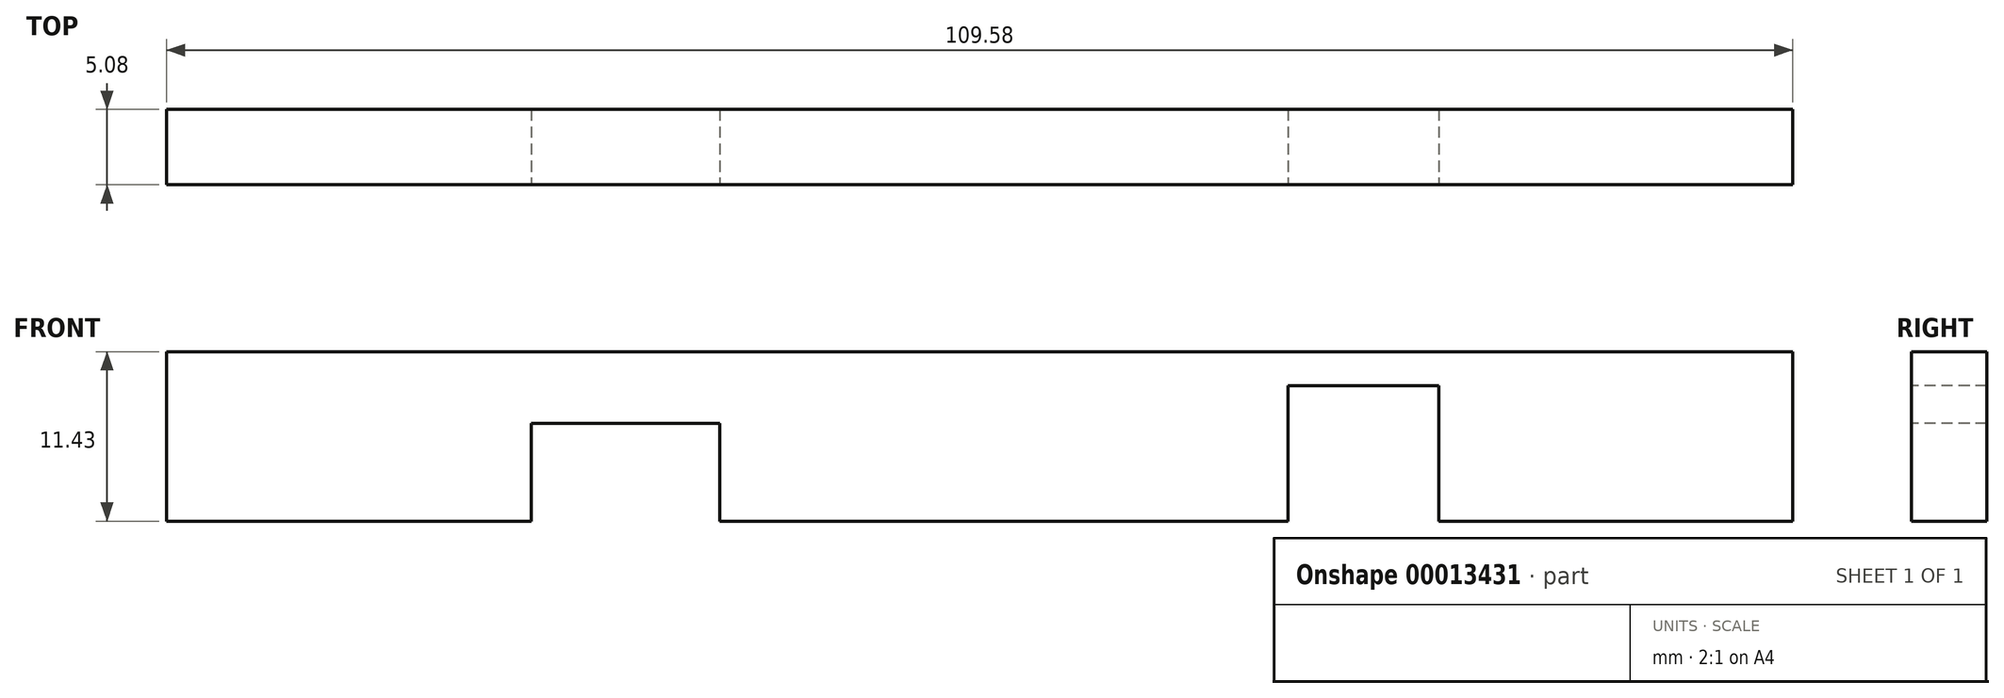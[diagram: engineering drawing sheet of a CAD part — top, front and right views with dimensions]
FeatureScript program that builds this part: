
annotation { "Feature Type Name" : "Feature", "Feature Type Description" : "" }
export const myFeature = defineFeature(function(context is Context, id is Id, definition is map)
    precondition{}
    {
        {
            var Q0;
            Q0=qCreatedBy(makeId("Front.planeOp"),FACE);
            var sketch = newSketch(context, id + "F0", { "sketchPlane" : qUnion([Q0])});
            skLineSegment(sketch, "E0.bottom", {"start": v(0, 0) * mm, "end": v(109.58, 0) * mm});
            skLineSegment(sketch, "E0.top", {"start": v(0, 11.43) * mm, "end": v(109.58, 11.43) * mm});
            skLineSegment(sketch, "E0.left", {"start": v(0, 0) * mm, "end": v(0, 11.43) * mm});
            skLineSegment(sketch, "E0.right", {"start": v(109.58, 0) * mm, "end": v(109.58, 11.43) * mm});
            skSolve(sketch);
        }
        {
            var Q0;
            Q0=qSketchRegion(id+"F0",true);
            extrude(context, id + "F1", {"entities" : qUnion([Q0]), "depth" : 5.08 * mm});
        }
        {
            var Q0;
            Q0=makeQuery(id+"F1.opExtrude","CAP_FACE",FACE,{"disambiguationData":[OSD([sQuery(id+"F0.wireOp",EDGE,"E0.bottom"),sQuery(id+"F0.wireOp",EDGE,"E0.top"),sQuery(id+"F0.wireOp",EDGE,"E0.left"),sQuery(id+"F0.wireOp",EDGE,"E0.right")])],"isStart":false});
            var sketch = newSketch(context, id + "F2", { "sketchPlane" : qUnion([Q0])});
            skLineSegment(sketch, "E1.bottom", {"start": v(24.59, 0) * mm, "end": v(37.29, 0) * mm});
            skLineSegment(sketch, "E1.top", {"start": v(24.59, 6.6) * mm, "end": v(37.29, 6.6) * mm});
            skLineSegment(sketch, "E1.left", {"start": v(24.59, 0) * mm, "end": v(24.59, 6.6) * mm});
            skLineSegment(sketch, "E1.right", {"start": v(37.29, 0) * mm, "end": v(37.29, 6.6) * mm});
            skLineSegment(sketch, "E2.bottom", {"start": v(75.6, 0) * mm, "end": v(85.75, 0) * mm});
            skLineSegment(sketch, "E2.top", {"start": v(75.6, 9.14) * mm, "end": v(85.75, 9.14) * mm});
            skLineSegment(sketch, "E2.left", {"start": v(75.6, 0) * mm, "end": v(75.6, 9.14) * mm});
            skLineSegment(sketch, "E2.right", {"start": v(85.75, 0) * mm, "end": v(85.75, 9.14) * mm});
            skSolve(sketch);
        }
        {
            var Q0;
            Q0 = qSketchRegion(id + "F2", true);
            extrude(context, id + "F3", {"entities" : qUnion([Q0]), "operationType" : NewBodyOperationType.REMOVE, "oppositeDirection" : true, "depth" : 25.4 * mm});
        }
    });
